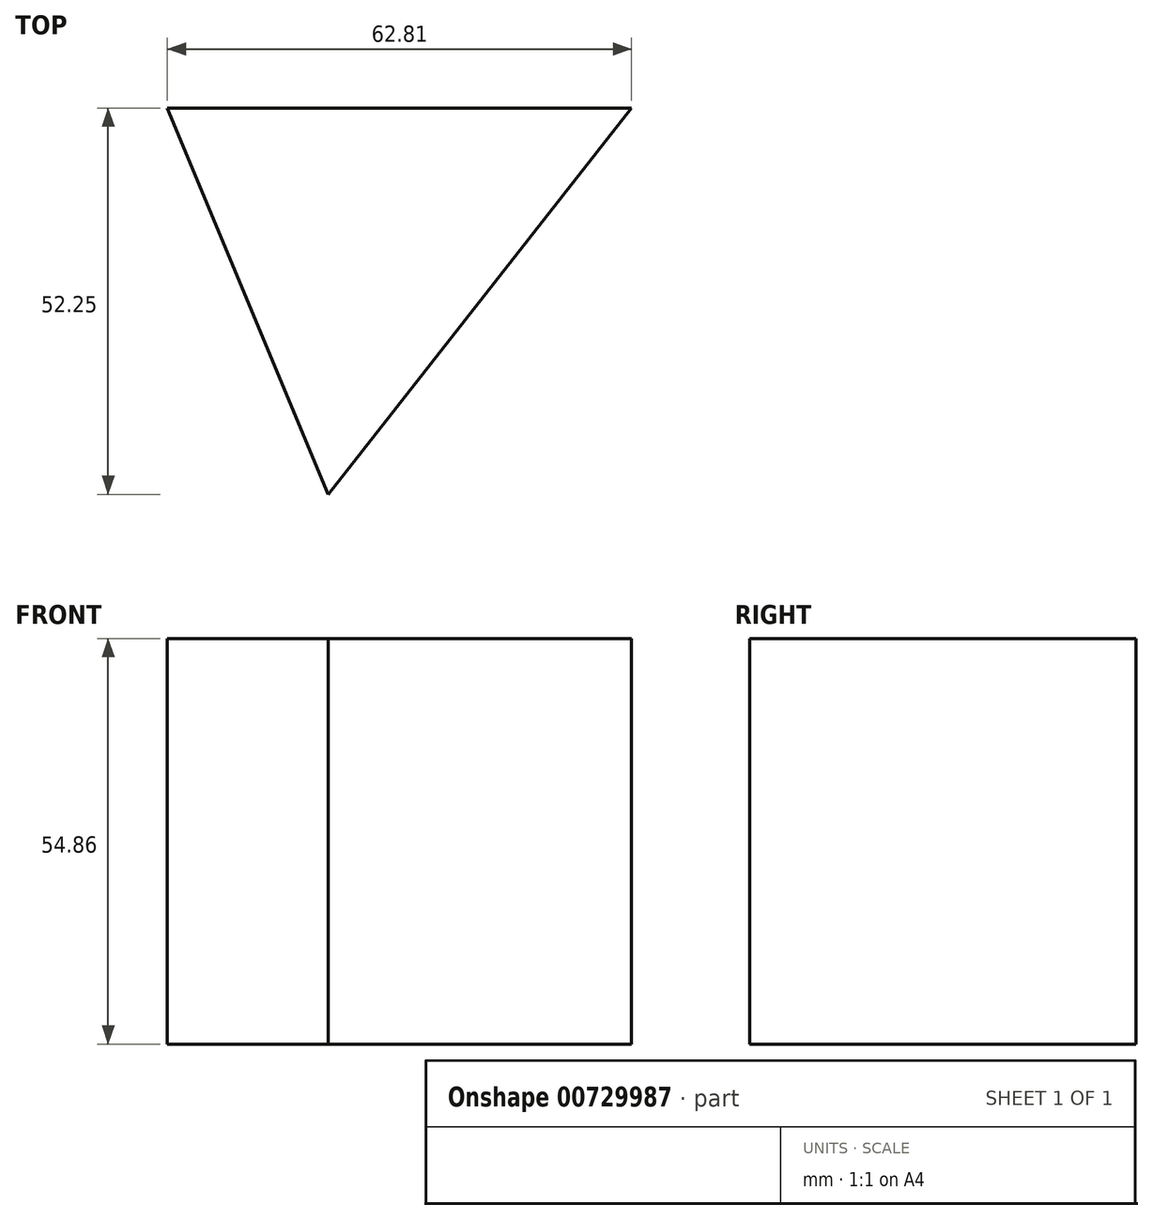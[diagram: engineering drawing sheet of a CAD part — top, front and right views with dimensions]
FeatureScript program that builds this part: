
annotation { "Feature Type Name" : "Feature", "Feature Type Description" : "" }
export const myFeature = defineFeature(function(context is Context, id is Id, definition is map)
    precondition{}
    {
        {
            var Q0;
            Q0=qCreatedBy(makeId("Top.planeOp"),FACE);
            var sketch = newSketch(context, id + "F0", { "sketchPlane" : qUnion([Q0])});
            skLineSegment(sketch, "E0", {"start": v(0, 0) * mm, "end": v(-62.8, 0) * mm});
            skLineSegment(sketch, "E1", {"start": v(-62.8, 0) * mm, "end": v(-41.05, -52.25) * mm});
            skLineSegment(sketch, "E2", {"start": v(-41.05, -52.25) * mm, "end": v(0, 0) * mm});
            skSolve(sketch);
        }
        {
            var Q0;
            Q0=makeQuery(id+"F0.imprint","IMPRINT",FACE,{"disambiguationData":[TD([[makeQuery(id+"F0.imprint","IMPRINT",EDGE,{"derivedFrom":sQuery(id+"F0.wireOp",EDGE,"E0")}),1.0]])]});
            extrude(context, id + "F1", {"entities" : qUnion([Q0]), "depth" : 54.86 * mm, "offsetDistance" : 25.4 * mm});
        }
    });
